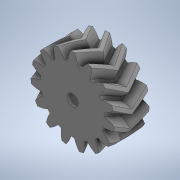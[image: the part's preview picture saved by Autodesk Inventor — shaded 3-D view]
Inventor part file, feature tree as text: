
AUTODESK INVENTOR PART (.ipt)
format: ipt  version: 2020 (Build 240168000, 168)  size: 532,992 bytes
history: native  units: mm (DEFAULTED — no unit token found)
features: plane x3, other x3, sketch x3, extrude x2, mirror x1
ambient origin geometry x8: Origin, YZ Plane, XZ Plane, XY Plane, X Axis, Y Axis, Z Axis, Center Point
bodies: Solid1 (feature_tree)
feature tree (12):
  extrude  "Extrusion1"  Depth=5.0mm TaperAngle=0.0deg
  plane  "Work Plane2"
  plane  "Work Plane8"
  plane  "Work Plane9"
  other  "Spur Gear"
  mirror  "Mirror1"
  extrude  "Extrusion2"  Depth=10.0mm TaperAngle=0.0deg
  sketch  "Sketch1"  dims[d0=24.099662mm d1=5.0mm d2=0.0mm]
  sketch  "Sketch2"  dims[d3=21.6mm d4=10.0mm d5=0.0mm]
  other  "Srf1"
  sketch  "Sketch3"  dims[d16=21.6mm d17=0.0mm d34=2.094395mm d39=0.0mm d41=0.0mm d43=21.6mm d46=21.6mm d47=0.0mm d48=0.0mm d49=3.2mm d50=10.0mm d51=0.0mm]
  other  "Pitch Diameter"
